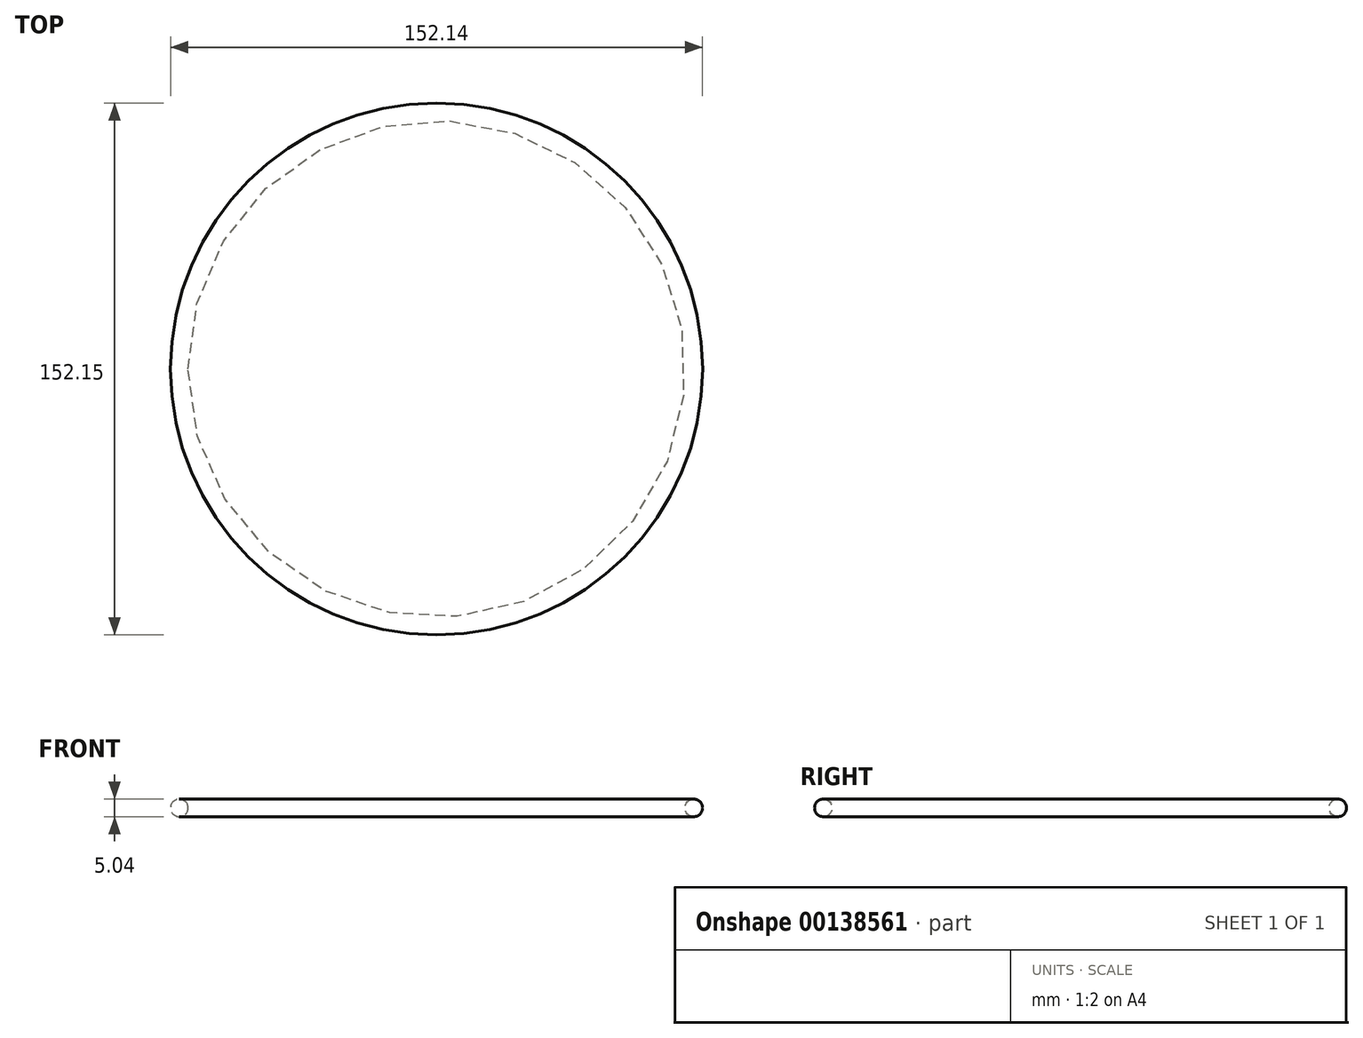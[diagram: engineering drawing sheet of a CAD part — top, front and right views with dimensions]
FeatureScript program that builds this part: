
annotation { "Feature Type Name" : "Feature", "Feature Type Description" : "" }
export const myFeature = defineFeature(function(context is Context, id is Id, definition is map)
    precondition{}
    {
        {
            var Q0;
            Q0=qCreatedBy(makeId("Right.planeOp"),FACE);
            var sketch = newSketch(context, id + "F0", { "sketchPlane" : qUnion([Q0])});
            skCircle(sketch, "E0", {"center": v(0, 0) * mm, "radius": 2.52 * mm});
            skLineSegment(sketch, "E1", {"start": v(73.56, 0) * mm, "end": v(73.56, 6.42) * mm});
            skPoint(sketch, "E2.start.orphan", {"position": v(2.52, 0) * mm});
            skSolve(sketch);
        }
        {
            var Q0;
            Q0=makeQuery(id+"F0.imprint","IMPRINT",FACE,{"disambiguationData":[TD([[makeQuery(id+"F0.imprint","IMPRINT",EDGE,{"derivedFrom":sQuery(id+"F0.wireOp",EDGE,"E0")}),1.0]])]});
            var Q1;
            Q1=sQuery(id+"F0.wireOp",EDGE,"E1");
            revolve(context, id + "F1", {"entities" : qUnion([Q0]), "axis" : qUnion([Q1]), "revolveType" : RevolveType.FULL});
        }
    });
